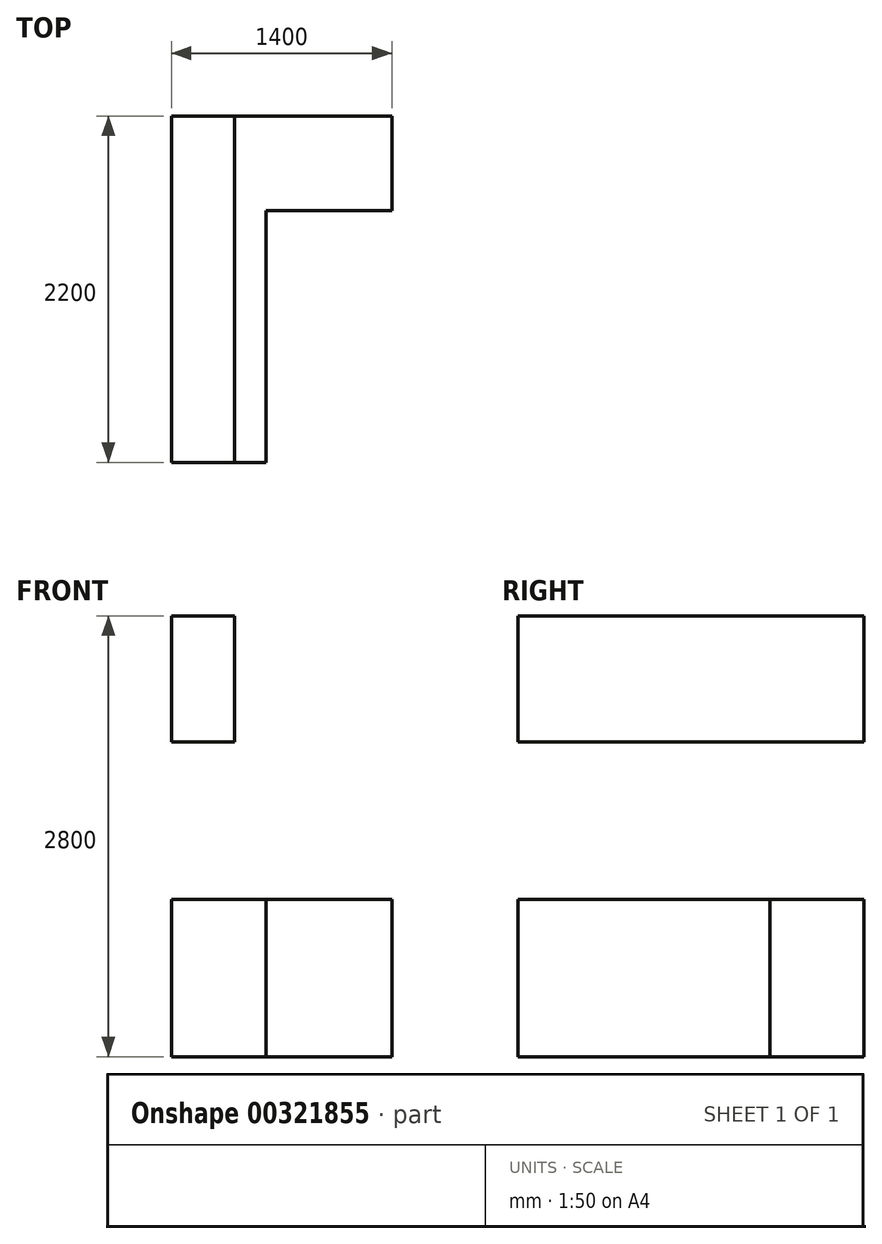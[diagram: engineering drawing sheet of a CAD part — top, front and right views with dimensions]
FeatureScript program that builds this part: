
annotation { "Feature Type Name" : "Feature", "Feature Type Description" : "" }
export const myFeature = defineFeature(function(context is Context, id is Id, definition is map)
    precondition{}
    {
        {
            var Q0;
            Q0=qCreatedBy(makeId("Top.planeOp"),FACE);
            var sketch = newSketch(context, id + "F0", { "sketchPlane" : qUnion([Q0])});
            skLineSegment(sketch, "E0", {"start": v(0, 0) * mm, "end": v(0, 2200) * mm});
            skLineSegment(sketch, "E1", {"start": v(0, 2200) * mm, "end": v(1400, 2200) * mm});
            skLineSegment(sketch, "E2", {"start": v(1400, 2200) * mm, "end": v(1400, 1600) * mm});
            skLineSegment(sketch, "E3", {"start": v(1400, 1600) * mm, "end": v(600, 1600) * mm});
            skLineSegment(sketch, "E4", {"start": v(600, 1600) * mm, "end": v(600, 0) * mm});
            skLineSegment(sketch, "E5", {"start": v(600, 0) * mm, "end": v(0, 0) * mm});
            skSolve(sketch);
        }
        {
            var Q0;
            Q0 = qSketchRegion(id + "F0", true);
            extrude(context, id + "F1", {"entities" : qUnion([Q0]), "depth" : 1000 * mm});
        }
        {
            var Q0;
            Q0=makeQuery(id+"F1.opExtrude","CAP_FACE",FACE,{"disambiguationData":[OSD([sQuery(id+"F0.wireOp",EDGE,"E0"),sQuery(id+"F0.wireOp",EDGE,"E1"),sQuery(id+"F0.wireOp",EDGE,"E2"),sQuery(id+"F0.wireOp",EDGE,"E3"),sQuery(id+"F0.wireOp",EDGE,"E4"),sQuery(id+"F0.wireOp",EDGE,"E5")])],"isStart":false});
            cPlane(context, id + "F2", {"entities" : qUnion([Q0]), "cplaneType" : CPlaneType.OFFSET, "offset" : 1000 * mm, "width" : 150 * mm, "height" : 150 * mm});
        }
        {
            var Q0;
            Q0=qCreatedBy(id+"F2.planeOp",FACE);
            var sketch = newSketch(context, id + "F3", { "sketchPlane" : qUnion([Q0])});
            skLineSegment(sketch, "E6.0", {"start": v(0, 0) * mm, "end": v(0, 2200) * mm});
            skLineSegment(sketch, "E7", {"start": v(400, 2200) * mm, "end": v(0, 2200) * mm});
            skLineSegment(sketch, "E8", {"start": v(400, 2200) * mm, "end": v(400, 0) * mm});
            skLineSegment(sketch, "E9", {"start": v(400, 0) * mm, "end": v(0, 0) * mm});
            skSolve(sketch);
        }
        {
            var Q0;
            Q0 = qSketchRegion(id + "F3", true);
            extrude(context, id + "F4", {"entities" : qUnion([Q0]), "depth" : 800 * mm});
        }
    });
